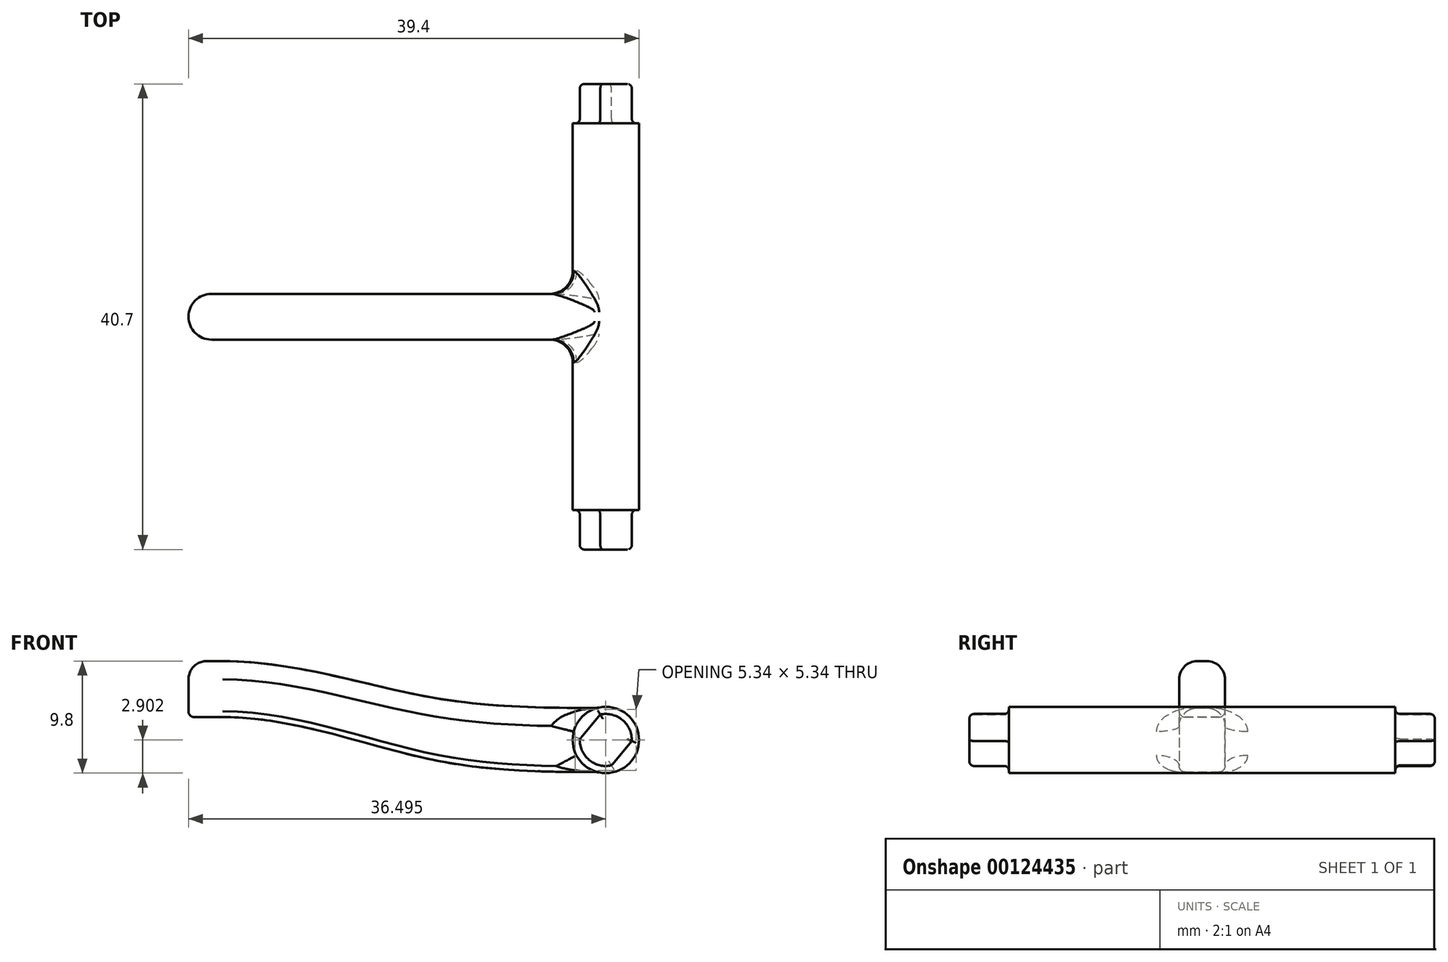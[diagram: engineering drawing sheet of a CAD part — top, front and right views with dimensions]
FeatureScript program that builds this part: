
annotation { "Feature Type Name" : "Feature", "Feature Type Description" : "" }
export const myFeature = defineFeature(function(context is Context, id is Id, definition is map)
    precondition{}
    {
        {
            var Q0;
            Q0=qCreatedBy(makeId("Front.planeOp"),FACE);
            var sketch = newSketch(context, id + "F0", { "sketchPlane" : qUnion([Q0])});
            skArc(sketch, "E0", {"start": v(-2.27, 0.1) * mm, "mid": v(-1.46, -1.74) * mm, "end": v(0.48, -2.22) * mm});
            skLineSegment(sketch, "E1", {"start": v(-2.27, 0.1) * mm, "end": v(-0.48, 2.22) * mm});
            skLineSegment(sketch, "E2", {"start": v(0.48, -2.22) * mm, "end": v(2.27, -0.1) * mm});
            skArc(sketch, "E3.trimOffspring", {"start": v(2.27, -0.1) * mm, "mid": v(1.46, 1.74) * mm, "end": v(-0.48, 2.22) * mm});
            skSolve(sketch);
        }
        {
            var Q0;
            Q0=qCreatedBy(makeId("Front.planeOp"),FACE);
            var sketch = newSketch(context, id + "F1", { "sketchPlane" : qUnion([Q0])});
            skCircle(sketch, "E4", {"center": v(0, 0) * mm, "radius": 2.9 * mm});
            skSolve(sketch);
        }
        {
            var Q0;
            Q0=qSketchRegion(id+"F1",true);
            extrude(context, id + "F2", {"entities" : qUnion([Q0]), "endBound" : BoundingType.SYMMETRIC, "depth" : 33.8 * mm});
        }
        {
            var Q0;
            Q0=qSketchRegion(id+"F0",true);
            extrude(context, id + "F3", {"entities" : qUnion([Q0]), "operationType" : NewBodyOperationType.ADD, "endBound" : BoundingType.SYMMETRIC, "depth" : 40.7 * mm});
        }
        {
            var Q0;
            Q0=qCreatedBy(makeId("Front.planeOp"),FACE);
            var sketch = newSketch(context, id + "F4", { "sketchPlane" : qUnion([Q0])});
            skPoint(sketch, "E5", {"position": v(-34.5, 2) * mm});
            skLineSegment(sketch, "E6", {"start": v(-34.5, 2) * mm, "end": v(-33.5, 2) * mm});
            skLineSegment(sketch, "E7", {"start": v(-2, 2.8) * mm, "end": v(-0.5, 2.8) * mm});
            skLineSegment(sketch, "E8", {"start": v(-0.5, 2.8) * mm, "end": v(-0.5, -2.8) * mm});
            skLineSegment(sketch, "E9", {"start": v(-0.5, -2.8) * mm, "end": v(-2, -2.8) * mm});
            skLineSegment(sketch, "E10", {"start": v(-34.5, 2) * mm, "end": v(-34.5, 6.9) * mm});
            skLineSegment(sketch, "E11", {"start": v(-34.5, 6.9) * mm, "end": v(-33.5, 6.9) * mm});
            skFitSpline(sketch, "E12", {"points": [v(-33.5, 6.9) * mm, v(-19, 4.5) * mm, v(-2, 2.8) * mm], "startDerivative": vector(31.17, 0) * mm, "endDerivative": vector(49.15, 0) * mm});
            skFitSpline(sketch, "E13", {"points": [v(-33.5, 2) * mm, v(-19, -0.8) * mm, v(-2, -2.8) * mm], "startDerivative": vector(31.15, 0) * mm, "endDerivative": vector(49.19, 0) * mm});
            skSolve(sketch);
        }
        {
            var Q0;
            Q0=makeQuery(id+"F4.imprint","IMPRINT",FACE,{"disambiguationData":[TD([[makeQuery(id+"F4.imprint","IMPRINT",EDGE,{"derivedFrom":sQuery(id+"F4.wireOp",EDGE,"E6")}),1.0]])]});
            extrude(context, id + "F5", {"entities" : qUnion([Q0]), "operationType" : NewBodyOperationType.ADD, "endBound" : BoundingType.SYMMETRIC, "depth" : 4 * mm});
        }
        {
            var Q0;
            Q0=makeQuery(id+"F5.opExtrude","SWEPT_FACE",FACE,{"disambiguationData":[OSD([sQuery(id+"F4.wireOp",EDGE,"E6")])]});
            var sketch = newSketch(context, id + "F6", { "sketchPlane" : qUnion([Q0])});
            skArc(sketch, "E14", {"start": v(-34.5, 2) * mm, "mid": v(-36.5, 0) * mm, "end": v(-34.5, -2) * mm});
            skLineSegment(sketch, "E15", {"start": v(-34.5, -2) * mm, "end": v(-34.5, 2) * mm});
            skSolve(sketch);
        }
        {
            var Q0;
            Q0=makeQuery(id+"F6.imprint","IMPRINT",FACE,{"disambiguationData":[TD([[makeQuery(id+"F6.imprint","IMPRINT",EDGE,{"derivedFrom":sQuery(id+"F6.wireOp",EDGE,"E14")}),1.0]])]});
            var Q1;
            Q1=makeQuery(id+"F5.opExtrude","SWEPT_FACE",FACE,{"disambiguationData":[OSD([sQuery(id+"F4.wireOp",EDGE,"E11")])]});
            extrude(context, id + "F7", {"entities" : qUnion([Q0]), "operationType" : NewBodyOperationType.ADD, "endBound" : BoundingType.UP_TO_SURFACE, "oppositeDirection" : true, "endBoundEntityFace" : qUnion([Q1]), "depth" : 25 * mm});
        }
        {
            var Q0;
            Q0=makeQuery(id+"F5.opExtrude","CAP_EDGE",EDGE,{"disambiguationData":[OSD([sQuery(id+"F4.wireOp",EDGE,"E13")])],"isStart":false});
            fillet(context, id + "F8", {"entities" : qUnion([Q0]), "radius" : 0.5 * mm, "tangentPropagation" : true, "allowEdgeOverflow" : false});
        }
        {
            var Q0;
            Q0=makeQuery(id+"F5.opExtrude","CAP_EDGE",EDGE,{"disambiguationData":[OSD([sQuery(id+"F4.wireOp",EDGE,"E12")])],"isStart":false});
            fillet(context, id + "F9", {"entities" : qUnion([Q0]), "radius" : 1.6 * mm, "tangentPropagation" : true, "allowEdgeOverflow" : false});
        }
        {
            var Q0;
            Q0=makeQuery(id+"F5.boolean.opBoolean","INTERSECT",EDGE,{"derivedFrom":[makeQuery(id+"F2.opExtrude","SWEPT_FACE",FACE,{"disambiguationData":[OSD([sQuery(id+"F1.wireOp",EDGE,"E4")])]}),makeQuery(id+"F5.opExtrude","CAP_FACE",FACE,{"disambiguationData":[OSD([sQuery(id+"F4.wireOp",EDGE,"E6"),sQuery(id+"F4.wireOp",EDGE,"E7"),sQuery(id+"F4.wireOp",EDGE,"E8"),sQuery(id+"F4.wireOp",EDGE,"E9"),sQuery(id+"F4.wireOp",EDGE,"E10"),sQuery(id+"F4.wireOp",EDGE,"E11"),sQuery(id+"F4.wireOp",EDGE,"E12"),sQuery(id+"F4.wireOp",EDGE,"E13")])],"isStart":false})]});
            fillet(context, id + "F10", {"entities" : qUnion([Q0]), "radius" : 2 * mm, "tangentPropagation" : true, "allowEdgeOverflow" : false});
        }
        {
            var Q0;
            Q0=makeQuery(id+"F3.opExtrude","CAP_EDGE",EDGE,{"disambiguationData":[OSD([sQuery(id+"F0.wireOp",EDGE,"E3.trimOffspring")])],"isStart":false});
            var Q1;
            Q1=makeQuery(id+"F3.opExtrude","CAP_EDGE",EDGE,{"disambiguationData":[OSD([sQuery(id+"F0.wireOp",EDGE,"E2")])],"isStart":false});
            var Q2;
            Q2=makeQuery(id+"F3.opExtrude","CAP_EDGE",EDGE,{"disambiguationData":[OSD([sQuery(id+"F0.wireOp",EDGE,"E0")])],"isStart":false});
            var Q3;
            Q3=makeQuery(id+"F3.opExtrude","CAP_EDGE",EDGE,{"disambiguationData":[OSD([sQuery(id+"F0.wireOp",EDGE,"E1")])],"isStart":false});
            var Q4;
            Q4=makeQuery(id+"F3.opExtrude","CAP_EDGE",EDGE,{"disambiguationData":[OSD([sQuery(id+"F0.wireOp",EDGE,"E0")])],"isStart":true});
            var Q5;
            Q5=makeQuery(id+"F3.opExtrude","CAP_EDGE",EDGE,{"disambiguationData":[OSD([sQuery(id+"F0.wireOp",EDGE,"E2")])],"isStart":true});
            var Q6;
            Q6=makeQuery(id+"F3.opExtrude","CAP_EDGE",EDGE,{"disambiguationData":[OSD([sQuery(id+"F0.wireOp",EDGE,"E3.trimOffspring")])],"isStart":true});
            var Q7;
            Q7=makeQuery(id+"F3.opExtrude","CAP_EDGE",EDGE,{"disambiguationData":[OSD([sQuery(id+"F0.wireOp",EDGE,"E1")])],"isStart":true});
            var Q8;
            Q8=makeQuery(id+"F3.boolean.opBoolean","INTERSECT",EDGE,{"derivedFrom":[makeQuery(id+"F2.opExtrude","CAP_FACE",FACE,{"disambiguationData":[OSD([sQuery(id+"F1.wireOp",EDGE,"E4")])],"isStart":true}),makeQuery(id+"F3.opExtrude","SWEPT_FACE",FACE,{"disambiguationData":[OSD([sQuery(id+"F0.wireOp",EDGE,"E2")])]})]});
            var Q9;
            Q9=makeQuery(id+"F3.boolean.opBoolean","INTERSECT",EDGE,{"derivedFrom":[makeQuery(id+"F2.opExtrude","CAP_FACE",FACE,{"disambiguationData":[OSD([sQuery(id+"F1.wireOp",EDGE,"E4")])],"isStart":true}),makeQuery(id+"F3.opExtrude","SWEPT_FACE",FACE,{"disambiguationData":[OSD([sQuery(id+"F0.wireOp",EDGE,"E3.trimOffspring")])]})]});
            var Q10;
            Q10=makeQuery(id+"F3.boolean.opBoolean","INTERSECT",EDGE,{"derivedFrom":[makeQuery(id+"F2.opExtrude","CAP_FACE",FACE,{"disambiguationData":[OSD([sQuery(id+"F1.wireOp",EDGE,"E4")])],"isStart":true}),makeQuery(id+"F3.opExtrude","SWEPT_FACE",FACE,{"disambiguationData":[OSD([sQuery(id+"F0.wireOp",EDGE,"E1")])]})]});
            var Q11;
            Q11=makeQuery(id+"F3.boolean.opBoolean","INTERSECT",EDGE,{"derivedFrom":[makeQuery(id+"F2.opExtrude","CAP_FACE",FACE,{"disambiguationData":[OSD([sQuery(id+"F1.wireOp",EDGE,"E4")])],"isStart":true}),makeQuery(id+"F3.opExtrude","SWEPT_FACE",FACE,{"disambiguationData":[OSD([sQuery(id+"F0.wireOp",EDGE,"E0")])]})]});
            var Q12;
            Q12=makeQuery(id+"F3.boolean.opBoolean","INTERSECT",EDGE,{"derivedFrom":[makeQuery(id+"F2.opExtrude","CAP_FACE",FACE,{"disambiguationData":[OSD([sQuery(id+"F1.wireOp",EDGE,"E4")])],"isStart":false}),makeQuery(id+"F3.opExtrude","SWEPT_FACE",FACE,{"disambiguationData":[OSD([sQuery(id+"F0.wireOp",EDGE,"E2")])]})]});
            var Q13;
            Q13=makeQuery(id+"F3.boolean.opBoolean","INTERSECT",EDGE,{"derivedFrom":[makeQuery(id+"F2.opExtrude","CAP_FACE",FACE,{"disambiguationData":[OSD([sQuery(id+"F1.wireOp",EDGE,"E4")])],"isStart":false}),makeQuery(id+"F3.opExtrude","SWEPT_FACE",FACE,{"disambiguationData":[OSD([sQuery(id+"F0.wireOp",EDGE,"E3.trimOffspring")])]})]});
            var Q14;
            Q14=makeQuery(id+"F3.boolean.opBoolean","INTERSECT",EDGE,{"derivedFrom":[makeQuery(id+"F2.opExtrude","CAP_FACE",FACE,{"disambiguationData":[OSD([sQuery(id+"F1.wireOp",EDGE,"E4")])],"isStart":false}),makeQuery(id+"F3.opExtrude","SWEPT_FACE",FACE,{"disambiguationData":[OSD([sQuery(id+"F0.wireOp",EDGE,"E1")])]})]});
            var Q15;
            {var subQ2=sQuery(id+"F0.wireOp",EDGE,"E0");Q15=makeQuery(id+"F3.boolean.opBoolean","SPLIT",FACE,{"disambiguationData":[TD([makeQuery(id+"F2.opExtrude","CAP_FACE",FACE,{"disambiguationData":[OSD([sQuery(id+"F1.wireOp",EDGE,"E4")])],"isStart":false})])],"derivedFrom":makeQuery(id+"F3.opExtrude","SWEPT_FACE",FACE,{"disambiguationData":[OSD([subQ2])]})});}
            fillet(context, id + "F11", {"entities" : qUnion([Q0, Q1, Q2, Q3, Q4, Q5, Q6, Q7, Q8, Q9, Q10, Q11, Q12, Q13, Q14, Q15]), "radius" : 0.4 * mm, "tangentPropagation" : true, "allowEdgeOverflow" : false});
        }
    });
